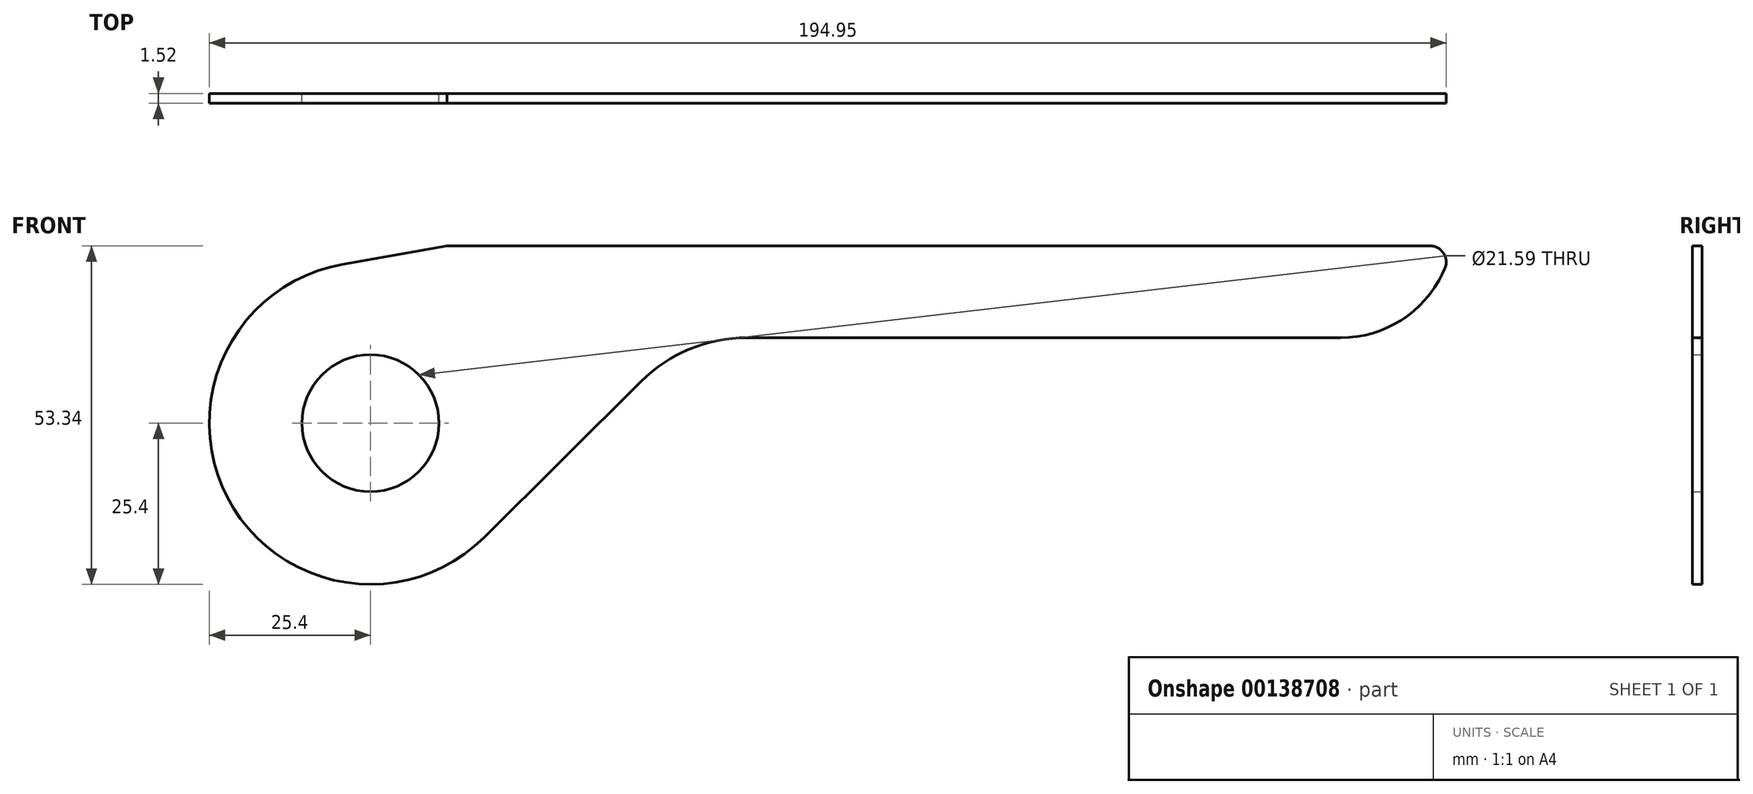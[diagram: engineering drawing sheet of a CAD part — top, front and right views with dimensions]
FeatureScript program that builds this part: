
annotation { "Feature Type Name" : "Feature", "Feature Type Description" : "" }
export const myFeature = defineFeature(function(context is Context, id is Id, definition is map)
    precondition{}
    {
        {
            var Q0;
            Q0=qCreatedBy(makeId("Front.planeOp"),FACE);
            var sketch = newSketch(context, id + "F0", { "sketchPlane" : qUnion([Q0])});
            skCircle(sketch, "E0", {"center": v(0, 0) * mm, "radius": 25.4 * mm});
            skLineSegment(sketch, "E1", {"start": v(-4.44, 25) * mm, "end": v(12.07, 27.94) * mm});
            skLineSegment(sketch, "E2", {"start": v(12.07, 27.94) * mm, "end": v(167.01, 27.94) * mm});
            skArc(sketch, "E3", {"start": v(169.3, 24.31) * mm, "mid": v(169.16, 26.76) * mm, "end": v(167.01, 27.94) * mm});
            skArc(sketch, "E4", {"start": v(152.91, 13.46) * mm, "mid": v(162.42, 16.22) * mm, "end": v(168.98, 23.62) * mm});
            skLineSegment(sketch, "E5", {"start": v(152.91, 13.46) * mm, "end": v(59.32, 13.46) * mm});
            skLineSegment(sketch, "E6", {"start": v(169.3, 24.31) * mm, "end": v(168.98, 23.62) * mm});
            skArc(sketch, "E7", {"start": v(59.32, 13.46) * mm, "mid": v(50.32, 11.68) * mm, "end": v(42.67, 6.6) * mm});
            skLineSegment(sketch, "E8", {"start": v(17.9, -18.02) * mm, "end": v(42.67, 6.6) * mm});
            skCircle(sketch, "E9", {"center": v(0, 0) * mm, "radius": 10.8 * mm});
            skSolve(sketch);
        }
        {
            var Q0;
            {var subQ0=sQuery(id+"F0.wireOp",EDGE,"E1");Q0=makeQuery(id+"F0.imprint","IMPRINT",FACE,{"disambiguationData":[TD([[makeQuery(id+"F0.imprint","IMPRINT",EDGE,{"derivedFrom":subQ0}),-1.0]])]});}
            var Q1;
            {var subQ0=sQuery(id+"F0.wireOp",EDGE,"E0");var subQ1=makeQuery(id+"F0.imprint","INTERSECT",VERTEX,{"derivedFrom":[subQ0,sQuery(id+"F0.wireOp",EDGE,"E1")]});Q1=makeQuery(id+"F0.imprint","IMPRINT",FACE,{"disambiguationData":[TD([[makeQuery(id+"F0.imprint","IMPRINT",EDGE,{"disambiguationData":[TD([[subQ1,-1.0]])],"derivedFrom":subQ0}),1.0]])]});}
            extrude(context, id + "F1", {"entities" : qUnion([Q0, Q1]), "depth" : 1.52 * mm});
        }
    });
